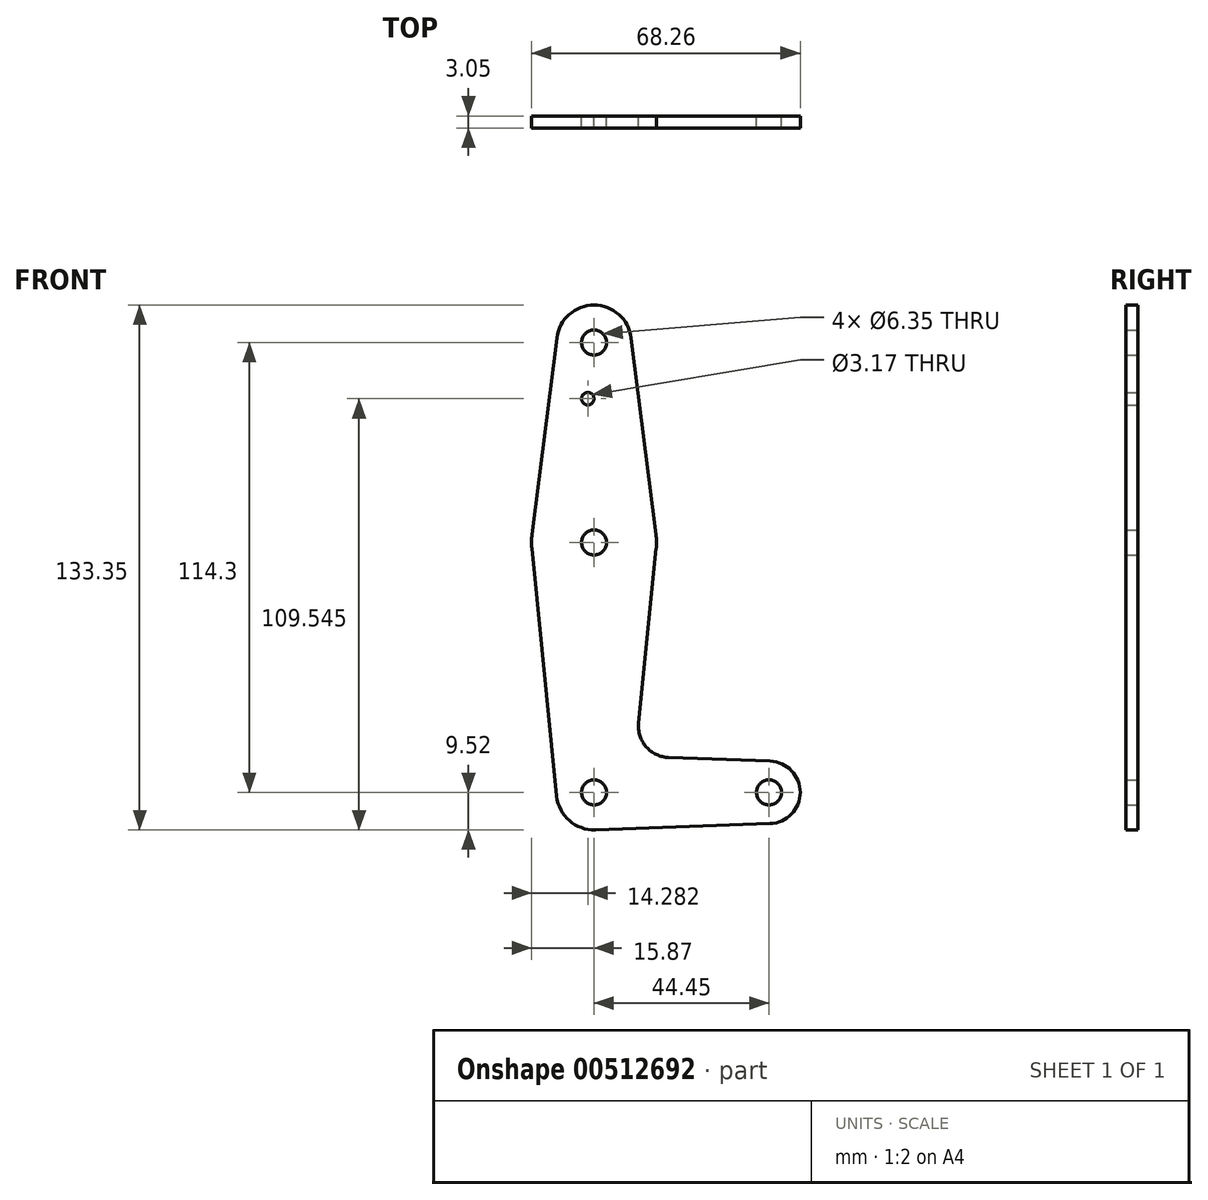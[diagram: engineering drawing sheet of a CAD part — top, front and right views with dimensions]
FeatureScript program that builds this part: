
annotation { "Feature Type Name" : "Feature", "Feature Type Description" : "" }
export const myFeature = defineFeature(function(context is Context, id is Id, definition is map)
    precondition{}
    {
        {
            var Q0;
            Q0=qCreatedBy(makeId("Front.planeOp"),FACE);
            var sketch = newSketch(context, id + "F0", { "sketchPlane" : qUnion([Q0])});
            skLineSegment(sketch, "E0", {"start": v(0, 0) * mm, "end": v(0, 114.3) * mm, "construction": true});
            skLineSegment(sketch, "E1", {"start": v(0, 0) * mm, "end": v(44.45, 0) * mm, "construction": true});
            skCircle(sketch, "E2", {"center": v(0, 114.3) * mm, "radius": 9.53 * mm});
            skCircle(sketch, "E3", {"center": v(0, 63.5) * mm, "radius": 15.88 * mm});
            skCircle(sketch, "E4", {"center": v(0, 0) * mm, "radius": 9.53 * mm});
            skCircle(sketch, "E5", {"center": v(44.45, 0) * mm, "radius": 7.94 * mm});
            skLineSegment(sketch, "E6", {"start": v(-9.45, 115.5) * mm, "end": v(-15.75, 65.48) * mm});
            skLineSegment(sketch, "E7", {"start": v(9.45, 115.5) * mm, "end": v(15.75, 65.48) * mm});
            skPoint(sketch, "E8.startSnap0", {"position": v(0, 57.15) * mm});
            skLineSegment(sketch, "E9", {"start": v(15.8, 61.91) * mm, "end": v(11.34, 17.6) * mm});
            skLineSegment(sketch, "E10", {"start": v(0, -9.53) * mm, "end": v(44.73, -7.93) * mm});
            skLineSegment(sketch, "E11", {"start": v(18.97, 8.85) * mm, "end": v(44.73, 7.93) * mm});
            skCircle(sketch, "E12", {"center": v(0, 114.3) * mm, "radius": 3.18 * mm});
            skCircle(sketch, "E13", {"center": v(-1.59, 100.03) * mm, "radius": 1.59 * mm});
            skCircle(sketch, "E14", {"center": v(0, 63.5) * mm, "radius": 3.18 * mm});
            skCircle(sketch, "E15", {"center": v(0, 0) * mm, "radius": 3.18 * mm});
            skCircle(sketch, "E16", {"center": v(44.45, 0) * mm, "radius": 3.18 * mm});
            skPoint(sketch, "E17.newPointB", {"position": v(0, 9.53) * mm});
            skArc(sketch, "E17.filletArc", {"start": v(11.34, 17.6) * mm, "mid": v(13.26, 11.57) * mm, "end": v(18.97, 8.85) * mm});
            skLineSegment(sketch, "E18", {"start": v(-15.8, 61.91) * mm, "end": v(-9.48, -0.95) * mm});
            skSolve(sketch);
        }
        {
            var Q0;
            Q0 = qSketchRegion(id + "F0", true);
            extrude(context, id + "F1", {"entities" : qUnion([Q0]), "depth" : 3.05 * mm});
        }
    });
